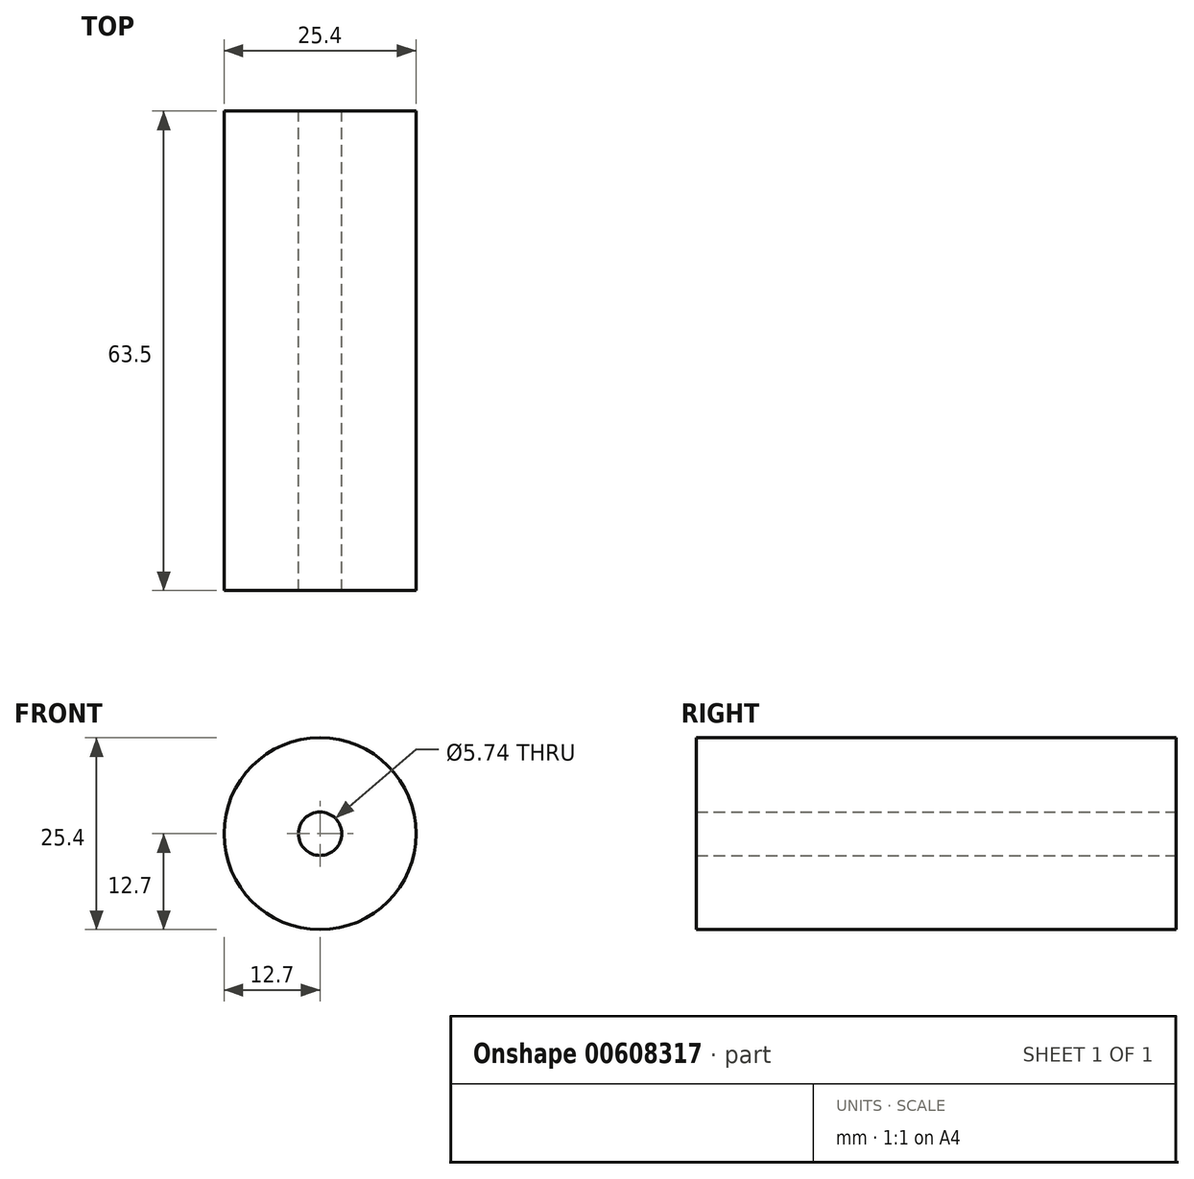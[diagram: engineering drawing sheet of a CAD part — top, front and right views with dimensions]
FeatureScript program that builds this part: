
annotation { "Feature Type Name" : "Feature", "Feature Type Description" : "" }
export const myFeature = defineFeature(function(context is Context, id is Id, definition is map)
    precondition{}
    {
        {
            var Q0;
            Q0=qCreatedBy(makeId("Front.planeOp"),FACE);
            var sketch = newSketch(context, id + "F0", { "sketchPlane" : qUnion([Q0])});
            skCircle(sketch, "E0", {"center": v(0, 0) * mm, "radius": 12.7 * mm});
            skSolve(sketch);
        }
        {
            var Q0;
            Q0=makeQuery(id+"F0.imprint","IMPRINT",FACE,{"disambiguationData":[TD([[makeQuery(id+"F0.imprint","IMPRINT",EDGE,{"derivedFrom":sQuery(id+"F0.wireOp",EDGE,"E0")}),1.0]])]});
            extrude(context, id + "F1", {"entities" : qUnion([Q0]), "depth" : 63.5 * mm, "offsetDistance" : 25.4 * mm});
        }
        {
            var Q0;
            Q0=makeQuery(id+"F1.opExtrude","CAP_FACE",FACE,{"disambiguationData":[OSD([sQuery(id+"F0.wireOp",EDGE,"E0")])],"isStart":true});
            var sketch = newSketch(context, id + "F2", { "sketchPlane" : qUnion([Q0])});
            skPoint(sketch, "E1", {"position": v(0, 0) * mm});
            skSolve(sketch);
        }
        {
            var Q0;
            Q0=sQuery(id+"F2.wireOp",VERTEX,"E1");
            var Q1;
            Q1=makeQuery(id+"F1.opExtrude","SWEPT_BODY",BODY,{"disambiguationData":[OSD([sQuery(id+"F0.wireOp",EDGE,"E0")])]});
            hole(context, id + "F3", {"style" : HoleStyle.SIMPLE, "endStyle" : HoleEndStyle.BLIND, "holeDiameter" : 5.74 * mm, "majorDiameter" : 6.35 * mm, "holeDepth" : 63.5 * mm, "isTappedThrough" : true, "tappedDepth" : 12.7 * mm, "tapClearance" : 3, "startFromSketch" : true, "locations" : qUnion([Q0]), "scope" : qUnion([Q1])});
        }
    });
